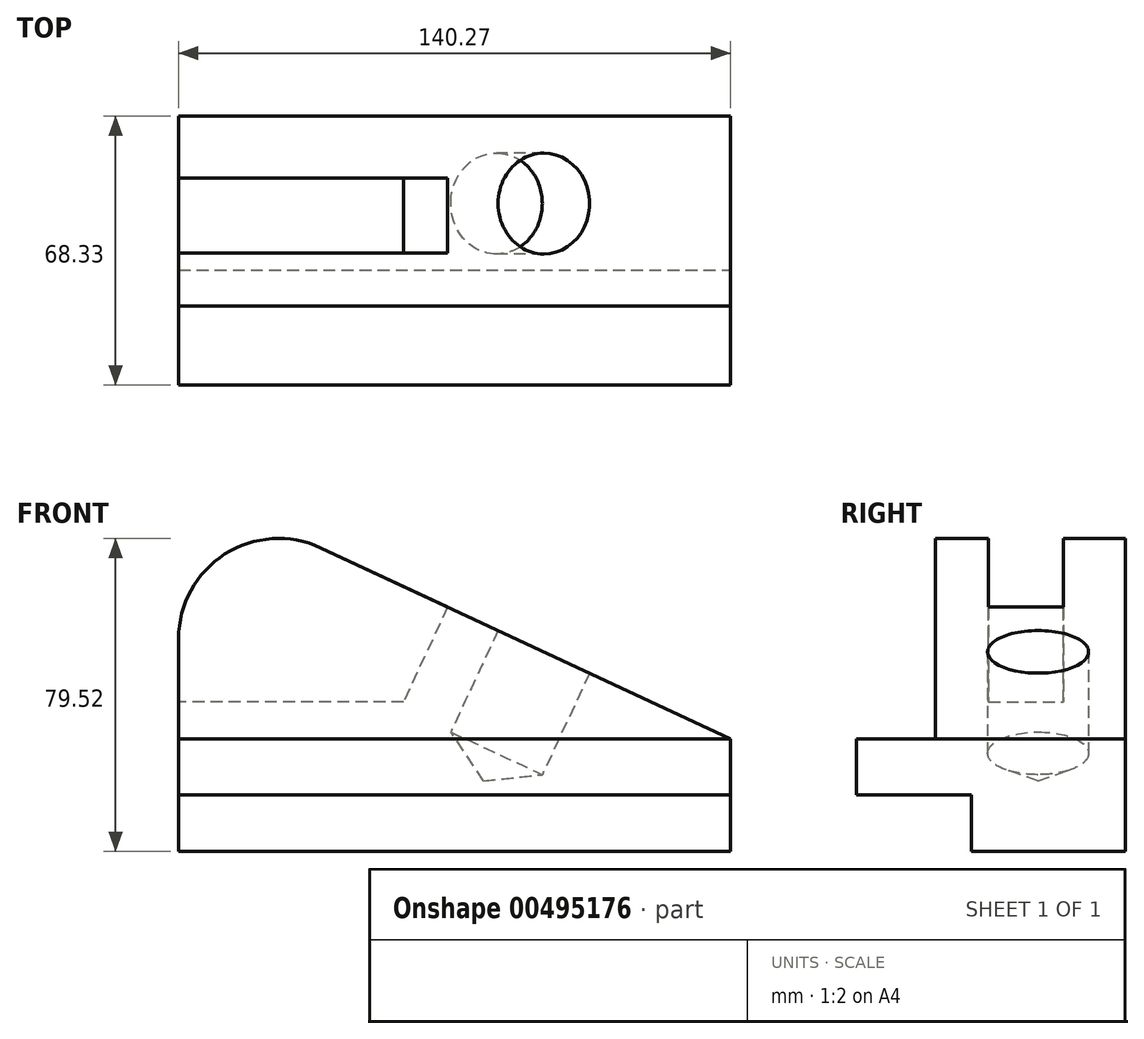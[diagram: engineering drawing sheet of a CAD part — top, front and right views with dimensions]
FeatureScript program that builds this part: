
annotation { "Feature Type Name" : "Feature", "Feature Type Description" : "" }
export const myFeature = defineFeature(function(context is Context, id is Id, definition is map)
    precondition{}
    {
        {
            var Q0;
            Q0=qCreatedBy(makeId("Front.planeOp"),FACE);
            var sketch = newSketch(context, id + "F0", { "sketchPlane" : qUnion([Q0])});
            skLineSegment(sketch, "E0.top", {"start": v(-308.64, 73.27) * mm, "end": v(-168.37, 73.27) * mm});
            skLineSegment(sketch, "E0.left", {"start": v(-308.64, 127.39) * mm, "end": v(-308.64, 73.27) * mm});
            skLineSegment(sketch, "E0.right", {"start": v(-168.37, 101.85) * mm, "end": v(-168.37, 73.27) * mm});
            skLineSegment(sketch, "E1", {"start": v(-168.37, 101.85) * mm, "end": v(-272.5, 150.4) * mm});
            skPoint(sketch, "E2.visualSharp", {"position": v(-308.64, 144.81) * mm});
            skPoint(sketch, "E3.visualSharp", {"position": v(-308.64, 152.77) * mm});
            skArc(sketch, "E3.filletArc", {"start": v(-272.5, 150.4) * mm, "mid": v(-296.9, 148.8) * mm, "end": v(-308.64, 127.39) * mm});
            skSolve(sketch);
        }
        {
            var Q0;
            Q0 = qSketchRegion(id + "F0", true);
            extrude(context, id + "F1", {"entities" : qUnion([Q0]), "depth" : 68.33 * mm});
        }
        {
            var Q0;
            Q0=makeQuery(id+"F1.opExtrude","SWEPT_FACE",FACE,{"disambiguationData":[OSD([sQuery(id+"F0.wireOp",EDGE,"E0.right")])]});
            var sketch = newSketch(context, id + "F2", { "sketchPlane" : qUnion([Q0])});
            skPoint(sketch, "E4.endSnap0", {"position": v(-68.33, 87.56) * mm});
            skLineSegment(sketch, "E5", {"start": v(-76, 87.62) * mm, "end": v(-76, 101.85) * mm});
            skLineSegment(sketch, "E6", {"start": v(-48.26, 101.85) * mm, "end": v(-48.26, 161.3) * mm});
            skLineSegment(sketch, "E7", {"start": v(-48.26, 161.3) * mm, "end": v(-91.75, 161.3) * mm});
            skLineSegment(sketch, "E8", {"start": v(-91.75, 161.3) * mm, "end": v(-91.75, 73.27) * mm});
            skLineSegment(sketch, "E9", {"start": v(-76, 87.62) * mm, "end": v(-39.12, 87.62) * mm});
            skLineSegment(sketch, "E10", {"start": v(-39.12, 87.62) * mm, "end": v(-39.12, 73.27) * mm});
            skLineSegment(sketch, "E11", {"start": v(-39.12, 73.27) * mm, "end": v(-91.75, 73.27) * mm});
            skLineSegment(sketch, "E12", {"start": v(-76, 101.85) * mm, "end": v(-48.26, 101.85) * mm});
            skSolve(sketch);
        }
        {
            var Q0;
            Q0 = qSketchRegion(id + "F2", true);
            extrude(context, id + "F3", {"entities" : qUnion([Q0]), "operationType" : NewBodyOperationType.REMOVE, "endBound" : BoundingType.THROUGH_ALL, "oppositeDirection" : true, "depth" : 25.4 * mm});
        }
        {
            var Q0;
            Q0=makeQuery(id+"F1.opExtrude","CAP_FACE",FACE,{"disambiguationData":[OSD([sQuery(id+"F0.wireOp",EDGE,"E0.top"),sQuery(id+"F0.wireOp",EDGE,"E0.left"),sQuery(id+"F0.wireOp",EDGE,"E0.right"),sQuery(id+"F0.wireOp",EDGE,"E1"),sQuery(id+"F0.wireOp",EDGE,"E3.filletArc")])],"isStart":true});
            cPlane(context, id + "F4", {"entities" : qUnion([Q0]), "cplaneType" : CPlaneType.OFFSET, "offset" : 22.22 * mm, "oppositeDirection" : true, "width" : 152.4 * mm, "height" : 152.4 * mm});
        }
        {
            var Q0;
            Q0=qCreatedBy(id+"F4.planeOp",FACE);
            var sketch = newSketch(context, id + "F5", { "sketchPlane" : qUnion([Q0])});
            skLineSegment(sketch, "E13", {"start": v(214.7, 126.4) * mm, "end": v(231.12, 91.21) * mm});
            skLineSegment(sketch, "E14", {"start": v(226.82, 130.8) * mm, "end": v(239.49, 103.62) * mm});
            skLineSegment(sketch, "E15", {"start": v(231.12, 91.21) * mm, "end": v(239.49, 103.62) * mm});
            skLineSegment(sketch, "E16", {"start": v(214.7, 126.4) * mm, "end": v(226.82, 130.8) * mm});
            skSolve(sketch);
        }
        {
            var Q0;
            Q0 = qSketchRegion(id + "F5", true);
            var Q1;
            Q1=sQuery(id+"F5.wireOp",EDGE,"E13");
            revolve(context, id + "F6", {"operationType" : NewBodyOperationType.REMOVE, "entities" : qUnion([Q0]), "axis" : qUnion([Q1]), "revolveType" : RevolveType.FULL, "oppositeDirection" : true});
        }
        {
            var Q0;
            Q0=makeQuery(id+"F1.opExtrude","CAP_FACE",FACE,{"disambiguationData":[OSD([sQuery(id+"F0.wireOp",EDGE,"E0.top"),sQuery(id+"F0.wireOp",EDGE,"E0.left"),sQuery(id+"F0.wireOp",EDGE,"E0.right"),sQuery(id+"F0.wireOp",EDGE,"E1"),sQuery(id+"F0.wireOp",EDGE,"E3.filletArc")])],"isStart":true});
            cPlane(context, id + "F7", {"entities" : qUnion([Q0]), "cplaneType" : CPlaneType.OFFSET, "offset" : 15.75 * mm, "oppositeDirection" : true, "width" : 152.4 * mm, "height" : 152.4 * mm});
        }
        {
            var Q0;
            Q0=qCreatedBy(id+"F7.planeOp",FACE);
            var sketch = newSketch(context, id + "F8", { "sketchPlane" : qUnion([Q0])});
            skLineSegment(sketch, "E17", {"start": v(229.54, 158.4) * mm, "end": v(251.5, 111.32) * mm});
            skLineSegment(sketch, "E18", {"start": v(251.5, 111.32) * mm, "end": v(320.86, 111.32) * mm});
            skLineSegment(sketch, "E19", {"start": v(229.54, 158.4) * mm, "end": v(320.86, 158.4) * mm});
            skLineSegment(sketch, "E20", {"start": v(320.86, 158.4) * mm, "end": v(320.86, 111.32) * mm});
            skSolve(sketch);
        }
        {
            var Q0;
            Q0 = qSketchRegion(id + "F8", true);
            extrude(context, id + "F9", {"entities" : qUnion([Q0]), "operationType" : NewBodyOperationType.REMOVE, "oppositeDirection" : true, "depth" : 19.05 * mm});
        }
    });
